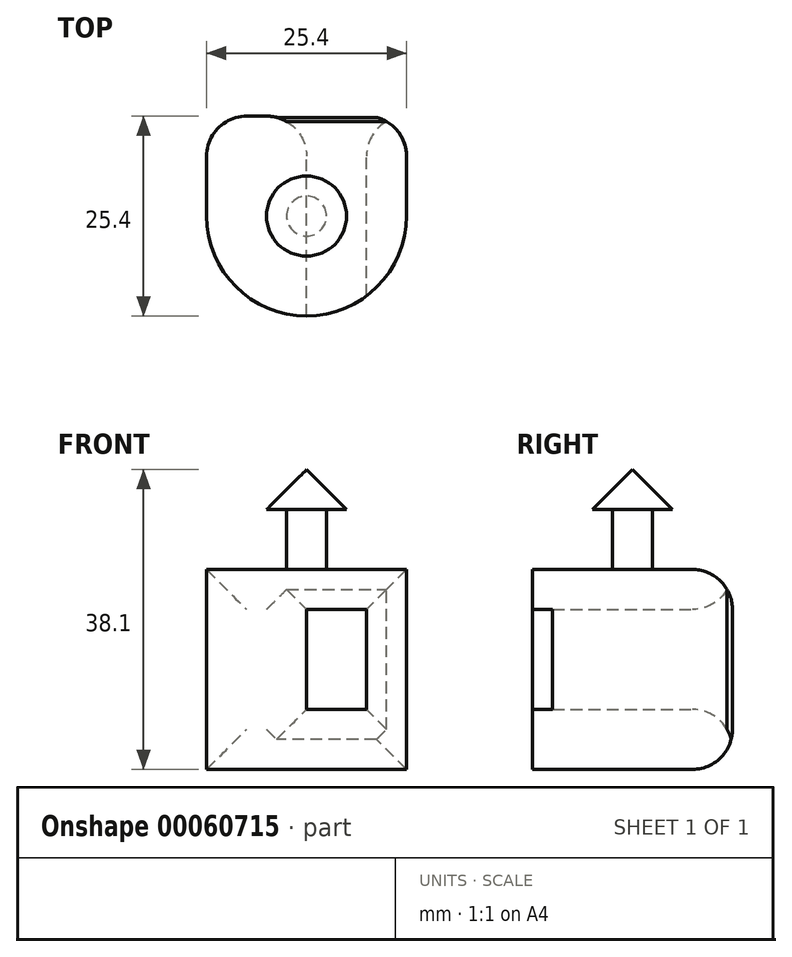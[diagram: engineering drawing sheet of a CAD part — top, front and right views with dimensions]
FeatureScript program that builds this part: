
annotation { "Feature Type Name" : "Feature", "Feature Type Description" : "" }
export const myFeature = defineFeature(function(context is Context, id is Id, definition is map)
    precondition{}
    {
        {
            var Q0;
            Q0=qCreatedBy(makeId("Top.planeOp"),FACE);
            var sketch = newSketch(context, id + "F0", { "sketchPlane" : qUnion([Q0])});
            skLineSegment(sketch, "E0.bottom", {"start": v(0, 0) * mm, "end": v(25.4, 0) * mm});
            skLineSegment(sketch, "E0.top", {"start": v(0, 25.4) * mm, "end": v(25.4, 25.4) * mm});
            skLineSegment(sketch, "E0.left", {"start": v(0, 0) * mm, "end": v(0, 25.4) * mm});
            skLineSegment(sketch, "E0.right", {"start": v(25.4, 0) * mm, "end": v(25.4, 25.4) * mm});
            skSolve(sketch);
        }
        {
            var Q0;
            Q0 = qSketchRegion(id + "F0", true);
            extrude(context, id + "F1", {"entities" : qUnion([Q0]), "depth" : 25.4 * mm});
        }
        {
            var Q0;
            Q0=makeQuery(id+"F1.opExtrude","SWEPT_EDGE",EDGE,{"disambiguationData":[OSD([sQuery(id+"F0.wireOp",EDGE,"E0.bottom"),sQuery(id+"F0.wireOp",EDGE,"E0.left")])]});
            var Q1;
            Q1=makeQuery(id+"F1.opExtrude","SWEPT_EDGE",EDGE,{"disambiguationData":[OSD([sQuery(id+"F0.wireOp",EDGE,"E0.bottom"),sQuery(id+"F0.wireOp",EDGE,"E0.right")])]});
            fillet(context, id + "F2", {"entities" : qUnion([Q0, Q1]), "radius" : 12.7 * mm, "tangentPropagation" : true, "allowEdgeOverflow" : false});
        }
        {
            var Q0;
            Q0=makeQuery(id+"F1.opExtrude","CAP_FACE",FACE,{"disambiguationData":[OSD([sQuery(id+"F0.wireOp",EDGE,"E0.bottom"),sQuery(id+"F0.wireOp",EDGE,"E0.top"),sQuery(id+"F0.wireOp",EDGE,"E0.left"),sQuery(id+"F0.wireOp",EDGE,"E0.right")])],"isStart":false});
            var sketch = newSketch(context, id + "F3", { "sketchPlane" : qUnion([Q0])});
            skCircle(sketch, "E1", {"center": v(12.7, 12.7) * mm, "radius": 2.54 * mm});
            skSolve(sketch);
        }
        {
            var Q0;
            Q0 = qSketchRegion(id + "F3", true);
            extrude(context, id + "F4", {"entities" : qUnion([Q0]), "operationType" : NewBodyOperationType.ADD, "depth" : 7.62 * mm});
        }
        {
            var Q0;
            Q0=makeQuery(id+"F4.opExtrude","CAP_FACE",FACE,{"disambiguationData":[OSD([sQuery(id+"F3.wireOp",EDGE,"E1")])],"isStart":false});
            var sketch = newSketch(context, id + "F5", { "sketchPlane" : qUnion([Q0])});
            skCircle(sketch, "E2", {"center": v(12.7, 12.7) * mm, "radius": 5.08 * mm});
            skSolve(sketch);
        }
        {
            var Q0;
            Q0 = qSketchRegion(id + "F5", true);
            extrude(context, id + "F6", {"entities" : qUnion([Q0]), "operationType" : NewBodyOperationType.ADD, "depth" : 5.08 * mm});
        }
        {
            var Q0;
            Q0=makeQuery(id+"F6.opExtrude","CAP_EDGE",EDGE,{"disambiguationData":[OSD([sQuery(id+"F5.wireOp",EDGE,"E2")])],"isStart":false});
            chamfer(context, id + "F7", {"entities" : qUnion([Q0]), "width" : 5.08 * mm, "tangentPropagation" : true});
        }
        {
            var Q0;
            Q0=makeQuery(id+"F1.opExtrude","SWEPT_FACE",FACE,{"disambiguationData":[OSD([sQuery(id+"F0.wireOp",EDGE,"E0.top")])]});
            var sketch = newSketch(context, id + "F8", { "sketchPlane" : qUnion([Q0])});
            skLineSegment(sketch, "E3.bottom", {"start": v(-20.32, 20.32) * mm, "end": v(-12.7, 20.32) * mm});
            skLineSegment(sketch, "E3.top", {"start": v(-20.32, 7.62) * mm, "end": v(-12.7, 7.62) * mm});
            skLineSegment(sketch, "E3.left", {"start": v(-20.32, 20.32) * mm, "end": v(-20.32, 7.62) * mm});
            skLineSegment(sketch, "E3.right", {"start": v(-12.7, 20.32) * mm, "end": v(-12.7, 7.62) * mm});
            skSolve(sketch);
        }
        {
            var Q0;
            Q0 = qSketchRegion(id + "F8", true);
            extrude(context, id + "F9", {"entities" : qUnion([Q0]), "operationType" : NewBodyOperationType.REMOVE, "oppositeDirection" : true, "depth" : 25.4 * mm});
        }
        {
            var Q0;
            Q0=makeQuery(id+"F1.opExtrude","SWEPT_FACE",FACE,{"disambiguationData":[OSD([sQuery(id+"F0.wireOp",EDGE,"E0.top")])]});
            fillet(context, id + "F10", {"entities" : qUnion([Q0]), "radius" : 5.08 * mm, "tangentPropagation" : true, "allowEdgeOverflow" : false});
        }
    });
